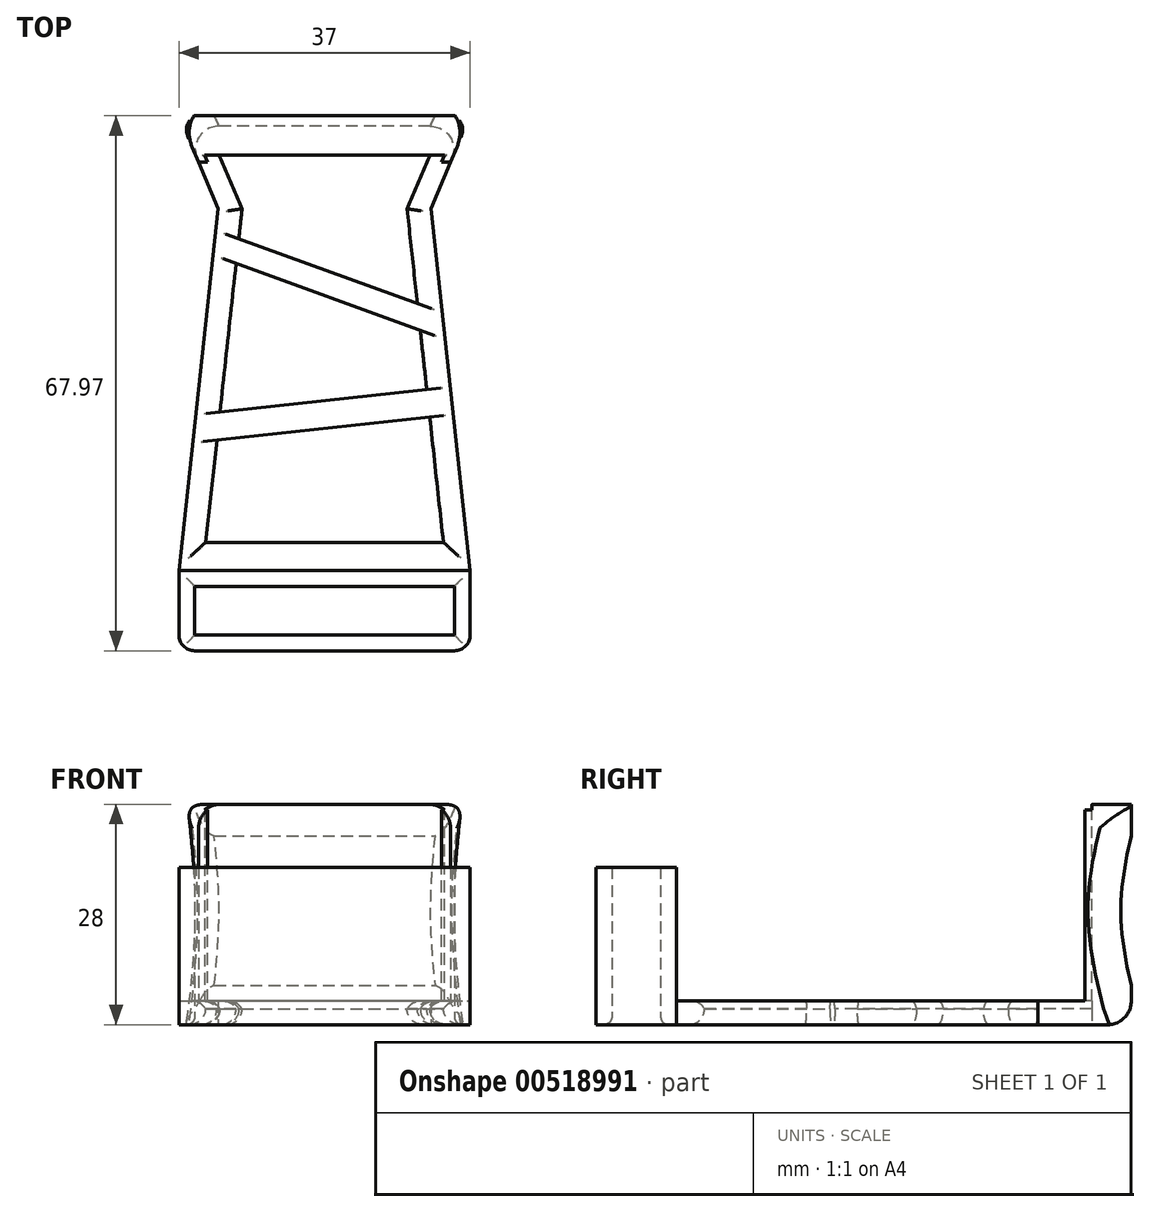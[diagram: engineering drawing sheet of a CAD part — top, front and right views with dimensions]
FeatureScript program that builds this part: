
annotation { "Feature Type Name" : "Feature", "Feature Type Description" : "" }
export const myFeature = defineFeature(function(context is Context, id is Id, definition is map)
    precondition{}
    {
        {
            var Q0;
            Q0=qCreatedBy(makeId("Top.planeOp"),FACE);
            var sketch = newSketch(context, id + "F0", { "sketchPlane" : qUnion([Q0])});
            skLineSegment(sketch, "E0.bottom", {"start": v(-16.62, 3.76) * mm, "end": v(16.38, 3.76) * mm});
            skLineSegment(sketch, "E0.top", {"start": v(-16.62, -2.44) * mm, "end": v(16.38, -2.44) * mm});
            skLineSegment(sketch, "E0.left", {"start": v(-16.62, 3.76) * mm, "end": v(-16.62, -2.44) * mm});
            skLineSegment(sketch, "E0.right", {"start": v(16.38, 3.76) * mm, "end": v(16.38, -2.44) * mm});
            skLineSegment(sketch, "E1.bottom", {"start": v(-18.62, 5.76) * mm, "end": v(18.38, 5.76) * mm});
            skLineSegment(sketch, "E1.top", {"start": v(-18.62, -4.44) * mm, "end": v(18.38, -4.44) * mm});
            skLineSegment(sketch, "E1.left", {"start": v(-18.62, 5.76) * mm, "end": v(-18.62, -4.44) * mm});
            skLineSegment(sketch, "E1.right", {"start": v(18.38, 5.76) * mm, "end": v(18.38, -4.44) * mm});
            skSolve(sketch);
        }
        {
            var Q0;
            Q0 = qSketchRegion(id + "F0", true);
            extrude(context, id + "F1", {"entities" : qUnion([Q0]), "depth" : 20 * mm, "offsetDistance" : 25 * mm});
        }
        {
            var Q0;
            Q0=makeQuery(id+"F1.opExtrude","SWEPT_EDGE",EDGE,{"disambiguationData":[OSD([sQuery(id+"F0.wireOp",EDGE,"E1.top"),sQuery(id+"F0.wireOp",EDGE,"E1.right")])]});
            var Q1;
            Q1=makeQuery(id+"F1.opExtrude","SWEPT_EDGE",EDGE,{"disambiguationData":[OSD([sQuery(id+"F0.wireOp",EDGE,"E1.top"),sQuery(id+"F0.wireOp",EDGE,"E1.left")])]});
            fillet(context, id + "F2", {"entities" : qUnion([Q0, Q1]), "radius" : 2 * mm, "tangentPropagation" : true, "allowEdgeOverflow" : false});
        }
        {
            var Q0;
            Q0=makeQuery(id+"F1.opExtrude","CAP_FACE",FACE,{"disambiguationData":[OSD([sQuery(id+"F0.wireOp",EDGE,"E0.bottom"),sQuery(id+"F0.wireOp",EDGE,"E0.top"),sQuery(id+"F0.wireOp",EDGE,"E0.left"),sQuery(id+"F0.wireOp",EDGE,"E0.right"),sQuery(id+"F0.wireOp",EDGE,"E1.bottom"),sQuery(id+"F0.wireOp",EDGE,"E1.top"),sQuery(id+"F0.wireOp",EDGE,"E1.left"),sQuery(id+"F0.wireOp",EDGE,"E1.right")])],"isStart":true});
            var sketch = newSketch(context, id + "F3", { "sketchPlane" : qUnion([Q0])});
            skLineSegment(sketch, "E2", {"start": v(-18.62, -5.76) * mm, "end": v(-13.62, -51.7) * mm});
            skLineSegment(sketch, "E3", {"start": v(-13.62, -51.7) * mm, "end": v(-18.62, -63.53) * mm});
            skLineSegment(sketch, "E4", {"start": v(-18.62, -63.53) * mm, "end": v(18.38, -63.53) * mm});
            skLineSegment(sketch, "E5", {"start": v(18.38, -63.53) * mm, "end": v(13.38, -51.7) * mm});
            skLineSegment(sketch, "E6", {"start": v(13.38, -51.7) * mm, "end": v(18.38, -5.76) * mm});
            skLineSegment(sketch, "E7", {"start": v(-15.22, -9.32) * mm, "end": v(-10.6, -51.7) * mm});
            skLineSegment(sketch, "E8", {"start": v(10.36, -51.7) * mm, "end": v(14.97, -9.32) * mm});
            skLineSegment(sketch, "E9", {"start": v(14.97, -9.32) * mm, "end": v(-15.22, -9.32) * mm});
            skLineSegment(sketch, "E10", {"start": v(-10.6, -51.7) * mm, "end": v(-13.5, -58.53) * mm});
            skLineSegment(sketch, "E11", {"start": v(-13.5, -58.53) * mm, "end": v(13.25, -58.53) * mm});
            skLineSegment(sketch, "E12", {"start": v(13.25, -58.53) * mm, "end": v(10.36, -51.7) * mm});
            skLineSegment(sketch, "E13", {"start": v(-11.02, -47.9) * mm, "end": v(11.67, -39.66) * mm});
            skLineSegment(sketch, "E14", {"start": v(11.67, -39.66) * mm, "end": v(12.04, -36.26) * mm});
            skLineSegment(sketch, "E15", {"start": v(12.04, -36.26) * mm, "end": v(-11.36, -44.76) * mm});
            skLineSegment(sketch, "E16", {"start": v(-13.41, -25.89) * mm, "end": v(12.86, -28.75) * mm});
            skLineSegment(sketch, "E17", {"start": v(12.86, -28.75) * mm, "end": v(13.24, -25.25) * mm});
            skLineSegment(sketch, "E18", {"start": v(13.24, -25.25) * mm, "end": v(-13.8, -22.3) * mm});
            skSolve(sketch);
        }
        {
            var Q0;
            Q0=makeQuery(id+"F3.imprint","IMPRINT",FACE,{"disambiguationData":[TD([[makeQuery(id+"F3.imprint","IMPRINT",EDGE,{"derivedFrom":sQuery(id+"F3.wireOp",EDGE,"E2")}),1.0]])]});
            var Q1;
            {var subQ0=sQuery(id+"F3.wireOp",EDGE,"E16");Q1=makeQuery(id+"F3.imprint","IMPRINT",FACE,{"disambiguationData":[TD([[makeQuery(id+"F3.imprint","IMPRINT",EDGE,{"derivedFrom":subQ0}),1.0]])]});}
            var Q2;
            {var subQ0=sQuery(id+"F3.wireOp",EDGE,"E13");Q2=makeQuery(id+"F3.imprint","IMPRINT",FACE,{"disambiguationData":[TD([[makeQuery(id+"F3.imprint","IMPRINT",EDGE,{"derivedFrom":subQ0}),1.0]])]});}
            extrude(context, id + "F4", {"entities" : qUnion([Q0, Q1, Q2]), "oppositeDirection" : true, "depth" : 3 * mm, "offsetDistance" : 25 * mm});
        }
        {
            var Q0;
            Q0=makeQuery(id+"F4.opExtrude","CAP_EDGE",EDGE,{"disambiguationData":[OSD([sQuery(id+"F3.wireOp",EDGE,"E8")])],"isStart":true});
            var Q1;
            Q1=makeQuery(id+"F4.opExtrude","CAP_EDGE",EDGE,{"disambiguationData":[OSD([sQuery(id+"F3.wireOp",EDGE,"E12")])],"isStart":true});
            var Q2;
            Q2=makeQuery(id+"F4.opExtrude","CAP_EDGE",EDGE,{"disambiguationData":[OSD([sQuery(id+"F3.wireOp",EDGE,"E10")])],"isStart":true});
            var Q3;
            Q3=makeQuery(id+"F4.opExtrude","CAP_EDGE",EDGE,{"disambiguationData":[OSD([sQuery(id+"F3.wireOp",EDGE,"E7")])],"isStart":true});
            var Q4;
            Q4=makeQuery(id+"F4.opExtrude","CAP_EDGE",EDGE,{"disambiguationData":[OSD([sQuery(id+"F3.wireOp",EDGE,"E9")])],"isStart":true});
            fillet(context, id + "F5", {"entities" : qUnion([Q0, Q1, Q2, Q3, Q4]), "radius" : 2 * mm, "tangentPropagation" : true, "allowEdgeOverflow" : false});
        }
        {
            var Q0;
            Q0=makeQuery(id+"F4.opExtrude","CAP_EDGE",EDGE,{"disambiguationData":[OSD([sQuery(id+"F3.wireOp",EDGE,"E7")])],"isStart":false});
            var Q1;
            Q1=makeQuery(id+"F4.opExtrude","CAP_EDGE",EDGE,{"disambiguationData":[OSD([sQuery(id+"F3.wireOp",EDGE,"E10")])],"isStart":false});
            var Q2;
            Q2=makeQuery(id+"F4.opExtrude","CAP_EDGE",EDGE,{"disambiguationData":[OSD([sQuery(id+"F3.wireOp",EDGE,"E12")])],"isStart":false});
            var Q3;
            Q3=makeQuery(id+"F4.opExtrude","CAP_EDGE",EDGE,{"disambiguationData":[OSD([sQuery(id+"F3.wireOp",EDGE,"E8")])],"isStart":false});
            var Q4;
            Q4=makeQuery(id+"F4.opExtrude","CAP_EDGE",EDGE,{"disambiguationData":[OSD([sQuery(id+"F3.wireOp",EDGE,"E9")])],"isStart":false});
            var Q5;
            {var subQ0=sQuery(id+"F3.wireOp",EDGE,"E11");Q5=makeQuery(id+"F5.opFillet","BLEND_EDGE",EDGE,{"blendedFrom":[makeQuery(id+"F4.opExtrude","CAP_EDGE",EDGE,{"disambiguationData":[OSD([subQ0])],"isStart":true}),makeQuery(id+"F4.opExtrude","SWEPT_FACE",FACE,{"disambiguationData":[OSD([subQ0])]})],"blendedInto":[makeQuery(id+"F4.opExtrude","SWEPT_FACE",FACE,{"disambiguationData":[OSD([subQ0])]})]});}
            fillet(context, id + "F6", {"entities" : qUnion([Q0, Q1, Q2, Q3, Q4, Q5]), "radius" : 2 * mm, "tangentPropagation" : true, "rho" : 0.5, "crossSection" : FilletCrossSection.CONIC, "allowEdgeOverflow" : false});
        }
        {
            var Q0;
            Q0=makeQuery(id+"F4.opExtrude","CAP_FACE",FACE,{"disambiguationData":[OSD([sQuery(id+"F0.wireOp",EDGE,"E1.bottom"),sQuery(id+"F3.wireOp",EDGE,"E2"),sQuery(id+"F3.wireOp",EDGE,"E3"),sQuery(id+"F3.wireOp",EDGE,"E4"),sQuery(id+"F3.wireOp",EDGE,"E5"),sQuery(id+"F3.wireOp",EDGE,"E6"),sQuery(id+"F3.wireOp",EDGE,"E7"),sQuery(id+"F3.wireOp",EDGE,"E8"),sQuery(id+"F3.wireOp",EDGE,"E9"),sQuery(id+"F3.wireOp",EDGE,"E10"),sQuery(id+"F3.wireOp",EDGE,"E11"),sQuery(id+"F3.wireOp",EDGE,"E12")])],"isStart":false});
            var sketch = newSketch(context, id + "F7", { "sketchPlane" : qUnion([Q0])});
            skLineSegment(sketch, "E19", {"start": v(-18.62, 63.53) * mm, "end": v(-16.12, 57.62) * mm});
            skLineSegment(sketch, "E20", {"start": v(-16.12, 57.62) * mm, "end": v(15.88, 57.62) * mm});
            skLineSegment(sketch, "E21", {"start": v(15.88, 57.62) * mm, "end": v(18.38, 63.53) * mm});
            skLineSegment(sketch, "E22", {"start": v(18.38, 63.53) * mm, "end": v(-18.62, 63.53) * mm});
            skPoint(sketch, "E23", {"position": v(-16.12, 57.62) * mm});
            skSolve(sketch);
        }
        {
            var Q0;
            {var subQ4=sQuery(id+"F7.wireOp",EDGE,"E19");Q0=makeQuery(id+"F7.imprint","IMPRINT",FACE,{"disambiguationData":[TD([[makeQuery(id+"F7.imprint","IMPRINT",EDGE,{"derivedFrom":subQ4}),-1.0]])]});}
            extrude(context, id + "F8", {"entities" : qUnion([Q0]), "operationType" : NewBodyOperationType.ADD, "depth" : 25 * mm, "offsetDistance" : 25 * mm});
        }
        {
            var Q0;
            Q0=qCreatedBy(makeId("Right.planeOp"),FACE);
            var sketch = newSketch(context, id + "F9", { "sketchPlane" : qUnion([Q0])});
            skFitSpline(sketch, "E24", {"points": [v(64.53, 27.87) * mm, v(62.5, 18.68) * mm, v(62.69, 9.11) * mm, v(64.53, 1.48) * mm], "startDerivative": vector(-4.5, -15.76) * mm, "endDerivative": vector(4.51, -11.35) * mm});
            skLineSegment(sketch, "E25", {"start": v(64.53, 27.87) * mm, "end": v(64.53, 1.48) * mm});
            skSolve(sketch);
        }
        {
            var Q0;
            Q0 = qSketchRegion(id + "F9", true);
            extrude(context, id + "F10", {"entities" : qUnion([Q0]), "operationType" : NewBodyOperationType.REMOVE, "oppositeDirection" : true, "depth" : 40 * mm, "offsetDistance" : 25 * mm, "symmetric" : true});
        }
        {
            var Q0;
            Q0=makeQuery(id+"F10.boolean.opBoolean","INTERSECT",EDGE,{"derivedFrom":[makeQuery(id+"F8.boolean.opBoolean","MERGE",FACE,{"derivedFrom":[makeQuery(id+"F4.opExtrude","SWEPT_FACE",FACE,{"disambiguationData":[OSD([sQuery(id+"F3.wireOp",EDGE,"E5")])]}),makeQuery(id+"F8.opExtrude","SWEPT_FACE",FACE,{"disambiguationData":[OSD([sQuery(id+"F7.wireOp",EDGE,"E21")])]})]}),makeQuery(id+"F10.opExtrude","SWEPT_FACE",FACE,{"disambiguationData":[OSD([sQuery(id+"F9.wireOp",EDGE,"E24")])]})]});
            var Q1;
            Q1=makeQuery(id+"F10.boolean.opBoolean","INTERSECT",EDGE,{"derivedFrom":[makeQuery(id+"F8.boolean.opBoolean","MERGE",FACE,{"derivedFrom":[makeQuery(id+"F4.opExtrude","SWEPT_FACE",FACE,{"disambiguationData":[OSD([sQuery(id+"F3.wireOp",EDGE,"E3")])]}),makeQuery(id+"F8.opExtrude","SWEPT_FACE",FACE,{"disambiguationData":[OSD([sQuery(id+"F7.wireOp",EDGE,"E19")])]})]}),makeQuery(id+"F10.opExtrude","SWEPT_FACE",FACE,{"disambiguationData":[OSD([sQuery(id+"F9.wireOp",EDGE,"E24")])]})]});
            var Q2;
            Q2=makeQuery(id+"F8.opExtrude","CAP_EDGE",EDGE,{"disambiguationData":[OSD([sQuery(id+"F7.wireOp",EDGE,"E19")])],"isStart":false});
            var Q3;
            Q3=makeQuery(id+"F8.opExtrude","CAP_EDGE",EDGE,{"disambiguationData":[OSD([sQuery(id+"F7.wireOp",EDGE,"E21")])],"isStart":false});
            var Q4;
            Q4=makeQuery(id+"F4.opExtrude","CAP_EDGE",EDGE,{"disambiguationData":[OSD([sQuery(id+"F3.wireOp",EDGE,"E4")])],"isStart":true});
            fillet(context, id + "F11", {"entities" : qUnion([Q0, Q1, Q2, Q3, Q4]), "radius" : 3 * mm, "tangentPropagation" : true, "allowEdgeOverflow" : false});
        }
        {
            var Q0;
            Q0=makeQuery(id+"F1.opExtrude","CAP_EDGE",EDGE,{"disambiguationData":[OSD([sQuery(id+"F0.wireOp",EDGE,"E0.bottom")])],"isStart":true});
            var Q1;
            Q1=makeQuery(id+"F1.opExtrude","CAP_EDGE",EDGE,{"disambiguationData":[OSD([sQuery(id+"F0.wireOp",EDGE,"E0.left")])],"isStart":true});
            var Q2;
            Q2=makeQuery(id+"F1.opExtrude","CAP_EDGE",EDGE,{"disambiguationData":[OSD([sQuery(id+"F0.wireOp",EDGE,"E0.top")])],"isStart":true});
            var Q3;
            Q3=makeQuery(id+"F1.opExtrude","CAP_EDGE",EDGE,{"disambiguationData":[OSD([sQuery(id+"F0.wireOp",EDGE,"E0.right")])],"isStart":true});
            fillet(context, id + "F12", {"entities" : qUnion([Q0, Q1, Q2, Q3]), "radius" : 1 * mm, "tangentPropagation" : true, "allowEdgeOverflow" : false});
        }
    });
